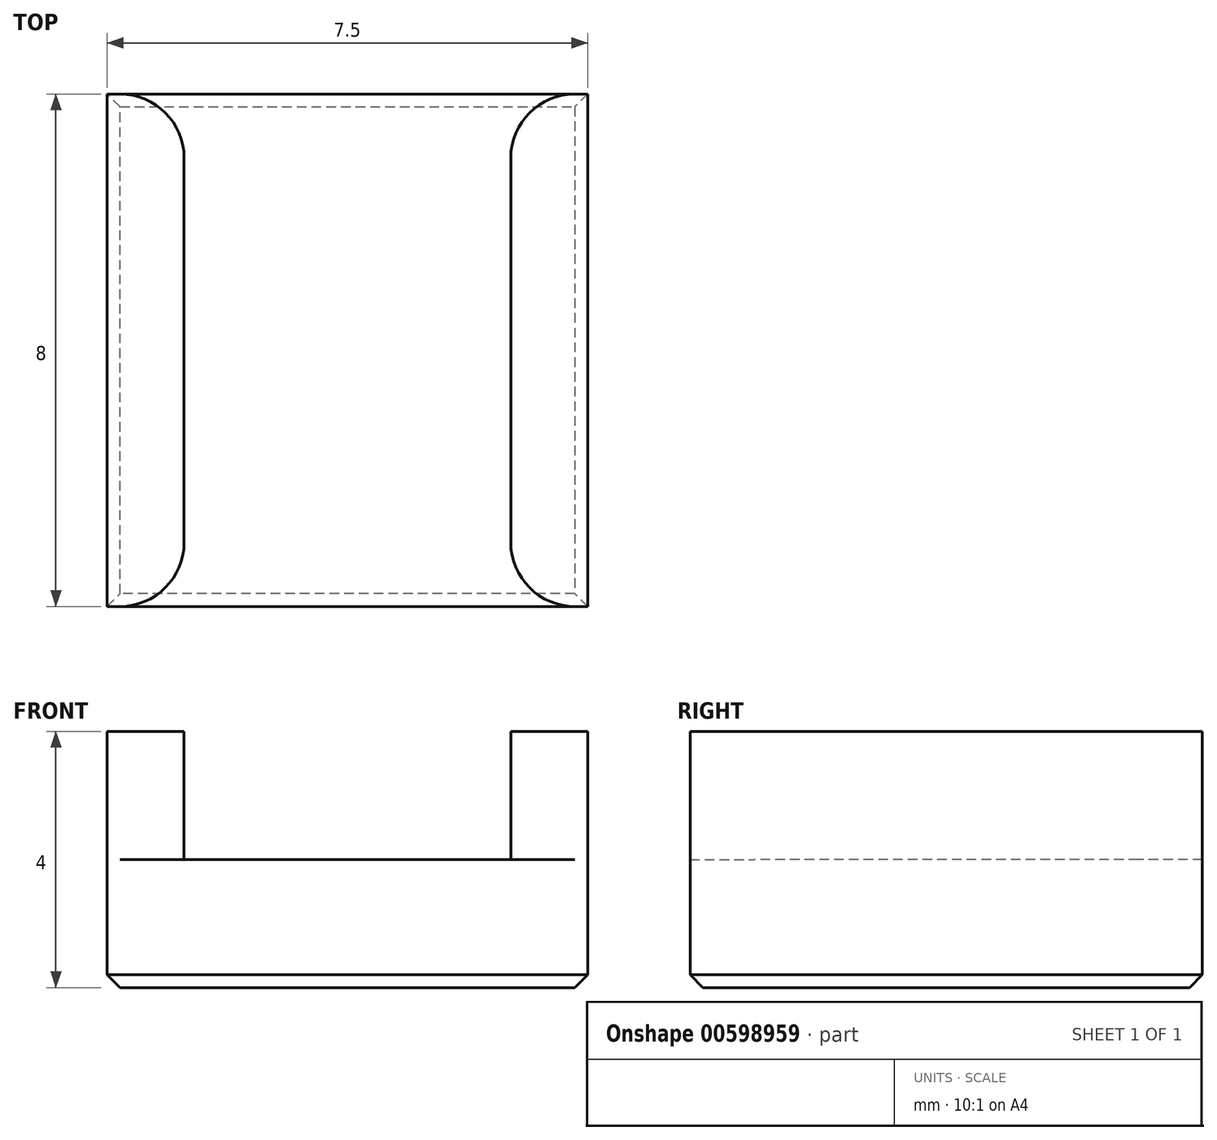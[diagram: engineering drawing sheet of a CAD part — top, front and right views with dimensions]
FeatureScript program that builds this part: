
annotation { "Feature Type Name" : "Feature", "Feature Type Description" : "" }
export const myFeature = defineFeature(function(context is Context, id is Id, definition is map)
    precondition{}
    {
        {
            var Q0;
            Q0=qCreatedBy(makeId("Front.planeOp"),FACE);
            var sketch = newSketch(context, id + "F0", { "sketchPlane" : qUnion([Q0])});
            skLineSegment(sketch, "E0", {"start": v(0, 0) * mm, "end": v(0, -2) * mm});
            skLineSegment(sketch, "E1", {"start": v(0, 0) * mm, "end": v(0, 2) * mm});
            skSolve(sketch);
        }
        {
            var Q0;
            Q0=qCreatedBy(makeId("Top.planeOp"),FACE);
            var sketch = newSketch(context, id + "F1", { "sketchPlane" : qUnion([Q0])});
            skLineSegment(sketch, "E2.bottom", {"start": v(2.55, 4) * mm, "end": v(-2.55, 4) * mm});
            skLineSegment(sketch, "E2.top", {"start": v(2.55, -4) * mm, "end": v(-2.55, -4) * mm});
            skLineSegment(sketch, "E2.left", {"start": v(2.55, 4) * mm, "end": v(2.55, -4) * mm});
            skLineSegment(sketch, "E2.right", {"start": v(-2.55, 4) * mm, "end": v(-2.55, -4) * mm});
            skPoint(sketch, "E2.middle", {"position": v(0, 0) * mm});
            skLineSegment(sketch, "E3", {"start": v(-2.55, 4) * mm, "end": v(-3.75, 4) * mm});
            skLineSegment(sketch, "E4", {"start": v(-3.75, 4) * mm, "end": v(-3.75, -4) * mm});
            skLineSegment(sketch, "E5", {"start": v(-3.75, -4) * mm, "end": v(-2.55, -4) * mm});
            skLineSegment(sketch, "E6", {"start": v(2.55, 4) * mm, "end": v(3.75, 4) * mm});
            skLineSegment(sketch, "E7", {"start": v(3.75, 4) * mm, "end": v(3.75, -4) * mm});
            skLineSegment(sketch, "E8", {"start": v(3.75, -4) * mm, "end": v(2.55, -4) * mm});
            skSolve(sketch);
        }
        {
            var Q0;
            Q0 = qSketchRegion(id + "F1", true);
            var Q1;
            Q1=sQuery(id+"F0.wireOp",EDGE,"E0");
            sweep(context, id + "F2", {"profiles" : qUnion([Q0]), "path" : qUnion([Q1])});
        }
        {
            var Q0;
            Q0=makeQuery(id+"F1.imprint","IMPRINT",FACE,{"disambiguationData":[TD([[makeQuery(id+"F1.imprint","IMPRINT",EDGE,{"derivedFrom":sQuery(id+"F1.wireOp",EDGE,"E2.right")}),-1.0]])]});
            var Q1;
            Q1=makeQuery(id+"F1.imprint","IMPRINT",FACE,{"disambiguationData":[TD([[makeQuery(id+"F1.imprint","IMPRINT",EDGE,{"derivedFrom":sQuery(id+"F1.wireOp",EDGE,"E2.left")}),1.0]])]});
            var Q2;
            Q2=sQuery(id+"F0.wireOp",EDGE,"E1");
            sweep(context, id + "F3", {"operationType" : NewBodyOperationType.ADD, "profiles" : qUnion([Q0, Q1]), "path" : qUnion([Q2])});
        }
        {
            var Q0;
            Q0=makeQuery(id+"F3.opSweep","SWEPT_EDGE",EDGE,{"disambiguationData":[OSD([sQuery(id+"F0.wireOp",EDGE,"E1"),sQuery(id+"F1.wireOp",EDGE,"E2.top"),sQuery(id+"F1.wireOp",EDGE,"E2.right"),sQuery(id+"F1.wireOp",EDGE,"E5")])]});
            var Q1;
            Q1=makeQuery(id+"F3.opSweep","SWEPT_EDGE",EDGE,{"disambiguationData":[OSD([sQuery(id+"F0.wireOp",EDGE,"E1"),sQuery(id+"F1.wireOp",EDGE,"E2.top"),sQuery(id+"F1.wireOp",EDGE,"E2.left"),sQuery(id+"F1.wireOp",EDGE,"E8")])]});
            var Q2;
            Q2=makeQuery(id+"F3.opSweep","SWEPT_EDGE",EDGE,{"disambiguationData":[OSD([sQuery(id+"F0.wireOp",EDGE,"E1"),sQuery(id+"F1.wireOp",EDGE,"E2.bottom"),sQuery(id+"F1.wireOp",EDGE,"E2.right"),sQuery(id+"F1.wireOp",EDGE,"E3")])]});
            var Q3;
            Q3=makeQuery(id+"F3.opSweep","SWEPT_EDGE",EDGE,{"disambiguationData":[OSD([sQuery(id+"F0.wireOp",EDGE,"E1"),sQuery(id+"F1.wireOp",EDGE,"E2.bottom"),sQuery(id+"F1.wireOp",EDGE,"E2.left"),sQuery(id+"F1.wireOp",EDGE,"E6")])]});
            fillet(context, id + "F4", {"entities" : qUnion([Q0, Q1, Q2, Q3]), "radius" : 1 * mm, "tangentPropagation" : true, "allowEdgeOverflow" : false});
        }
        {
            var Q0;
            Q0=makeQuery(id+"F2.opSweep","CAP_FACE",FACE,{"disambiguationData":[OSD([sQuery(id+"F0.wireOp",VERTEX,"E0.end"),sQuery(id+"F1.wireOp",EDGE,"E2.bottom"),sQuery(id+"F1.wireOp",EDGE,"E2.top"),sQuery(id+"F1.wireOp",EDGE,"E3"),sQuery(id+"F1.wireOp",EDGE,"E4"),sQuery(id+"F1.wireOp",EDGE,"E5"),sQuery(id+"F1.wireOp",EDGE,"E6"),sQuery(id+"F1.wireOp",EDGE,"E7"),sQuery(id+"F1.wireOp",EDGE,"E8")])],"isStart":false});
            chamfer(context, id + "F5", {"entities" : qUnion([Q0]), "width" : 0.2 * mm});
        }
    });
